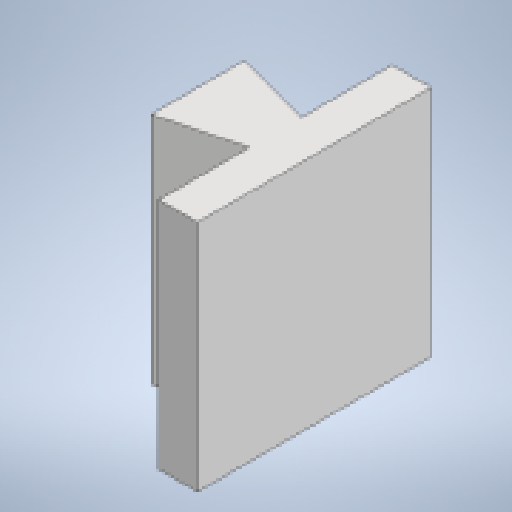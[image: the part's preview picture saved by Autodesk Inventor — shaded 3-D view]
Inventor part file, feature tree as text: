
AUTODESK INVENTOR PART (.ipt)
format: ipt  version: 2023 (Build 270158000, 158)  size: 124,416 bytes
history: native  units: mm
features: extrude x1, sketch x1
ambient origin geometry x8: Origin, YZ Plane, XZ Plane, XY Plane, X Axis, Y Axis, Z Axis, Center Point
bodies: Solid1 (feature_tree)
feature tree (2):
  extrude  "Extrusion1"  Depth=30.0mm
  sketch  "Sketch1"  dims[d0=30.0deg d1=12.0mm d2=30.0mm d3=10.0mm d4=5.0mm d5=30.0mm d6=0.0mm]
